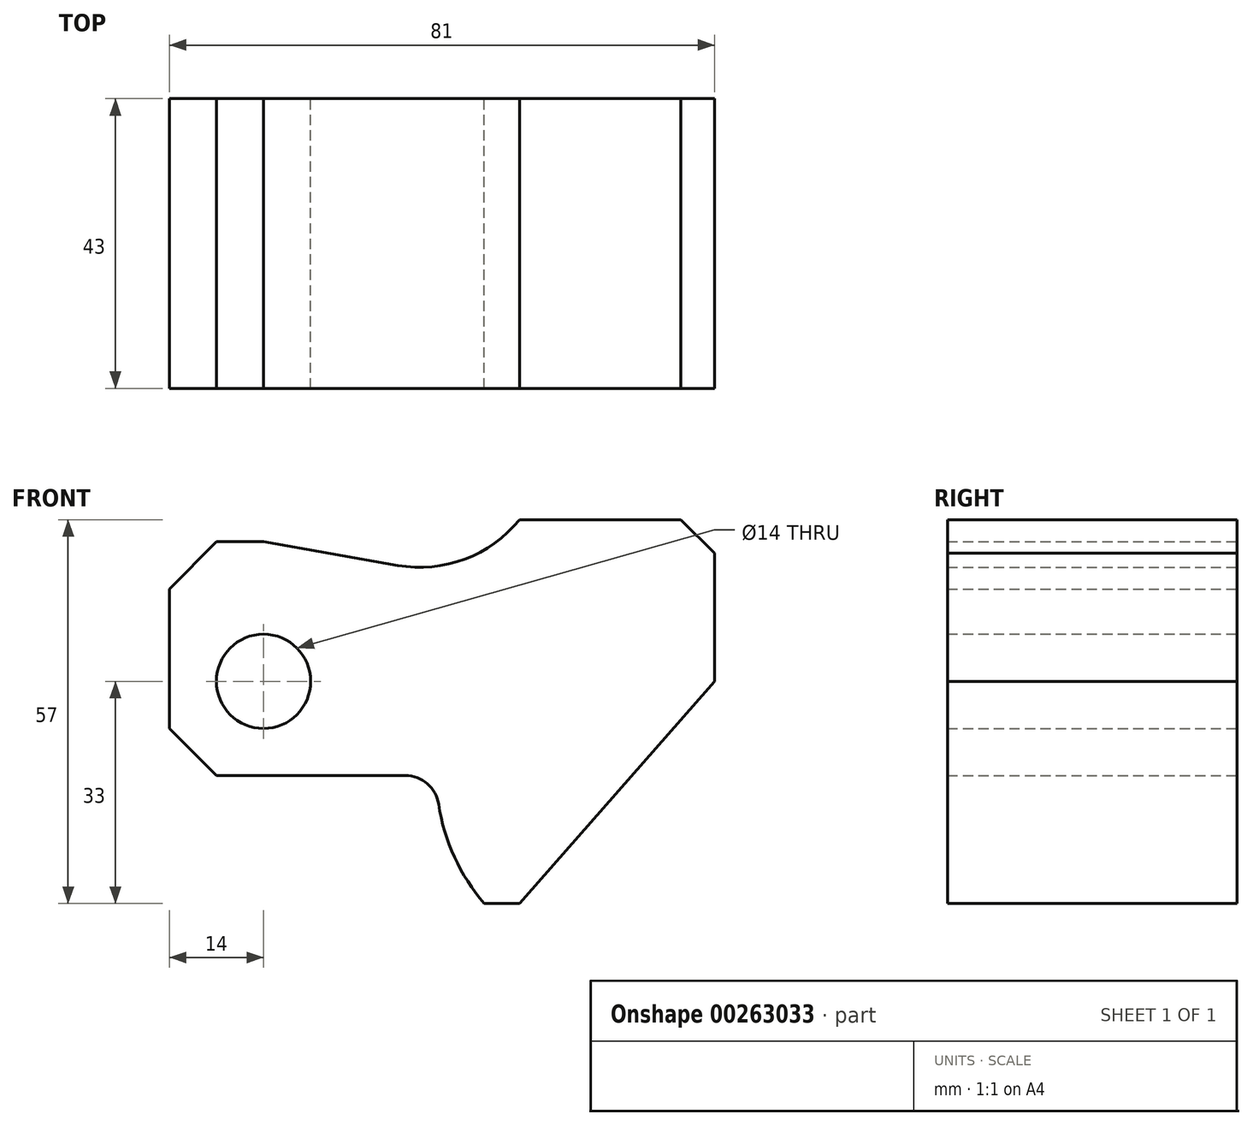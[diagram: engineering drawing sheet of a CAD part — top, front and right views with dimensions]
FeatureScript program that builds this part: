
annotation { "Feature Type Name" : "Feature", "Feature Type Description" : "" }
export const myFeature = defineFeature(function(context is Context, id is Id, definition is map)
    precondition{}
    {
        {
            var Q0;
            Q0=qCreatedBy(makeId("Front.planeOp"),FACE);
            var sketch = newSketch(context, id + "F0", { "sketchPlane" : qUnion([Q0])});
            skCircle(sketch, "E0", {"center": v(0, 0) * mm, "radius": 7 * mm});
            skLineSegment(sketch, "E1", {"start": v(-14, 13.72) * mm, "end": v(-14, -7) * mm});
            skLineSegment(sketch, "E2", {"start": v(-14, -7) * mm, "end": v(-7, -14) * mm});
            skLineSegment(sketch, "E3", {"start": v(-7, -14) * mm, "end": v(21.07, -14) * mm});
            skLineSegment(sketch, "E4", {"start": v(-14, 13.72) * mm, "end": v(-7, 20.72) * mm});
            skLineSegment(sketch, "E5", {"start": v(-7, 20.72) * mm, "end": v(0, 20.72) * mm});
            skLineSegment(sketch, "E6", {"start": v(0, 20.72) * mm, "end": v(19.9, 17.21) * mm});
            skArc(sketch, "E7", {"start": v(19.9, 17.21) * mm, "mid": v(29.88, 18.13) * mm, "end": v(38, 24) * mm});
            skArc(sketch, "E8", {"start": v(26.01, -18.26) * mm, "mid": v(24.33, -15.21) * mm, "end": v(21.07, -14) * mm});
            skArc(sketch, "E9", {"start": v(26.01, -18.26) * mm, "mid": v(28.35, -26.12) * mm, "end": v(32.79, -33) * mm});
            skLineSegment(sketch, "E10", {"start": v(32.79, -33) * mm, "end": v(38, -33) * mm});
            skLineSegment(sketch, "E11", {"start": v(38, -33) * mm, "end": v(67, 0) * mm});
            skLineSegment(sketch, "E12", {"start": v(67, 0) * mm, "end": v(67, 19) * mm});
            skLineSegment(sketch, "E13", {"start": v(67, 19) * mm, "end": v(62, 24) * mm});
            skLineSegment(sketch, "E14", {"start": v(62, 24) * mm, "end": v(38, 24) * mm});
            skSolve(sketch);
        }
        {
            var Q0;
            Q0=makeQuery(id+"F0.imprint","IMPRINT",FACE,{"disambiguationData":[TD([[makeQuery(id+"F0.imprint","IMPRINT",EDGE,{"derivedFrom":sQuery(id+"F0.wireOp",EDGE,"E0")}),-1.0]])]});
            extrude(context, id + "F1", {"entities" : qUnion([Q0]), "depth" : 43 * mm});
        }
    });
